# Revit family: HV3 für Kältefestpunkt_
name_source: partatom
category: Allgemeines Modell
revit_build: Autodesk Revit 2017 (Build: 20190508_0315(x64)
units: mm (PartAtom-declared; Revit-internal decimal feet)

## family parameters
Basisbauteil = Fläche
Beim Laden mit Abzugskörper schneiden = Nein
Bemaßung runder Anschluss = Durchmesser verwenden
Gemeinsam genutzt = Ja
Kann Basisbauteil für Bewehrung sein = Nein
Raumberechnungspunkt = Nein
Teiletyp = Normal

## types (2) — shared parameters
Anzahl Rohrschellen = 3
Anzugsmoment Hammersperrkopf = 120 Nm
Artikelnummer = 00200407/fvz
Breite Material Rohrschelle = 50 mm
EAN = 4250928400024
Fabrikat = MEFA
Gewicht = 5.68 kg
Kurztext1 = Festpunkthalterung HV 3
Kurztext2 = 64 - 406 mm Fx 30 kN 164 - 216 mm
Länge = 160 mm  [stored 0.524934 ft]
Mengeneinheit = St
Rohrschellentyp = Titan HD
Stärke Material Rohrschelle = 5 mm
Vorgabe-Ansicht = 1219 mm
max. Achshöhe = 216 mm
max. Rohraußendurchmesser = 406 mm  [stored 1.33202 ft]
max. zul. Last Fx = 6.74 kip
max. zul. Last Fz = 4.05 kip
max. zul. Last Fz mit 3 Schellen = 40 kN
min. Achshöhe = 164 mm
min. Rohraußendurchmesser = 64 mm  [stored 0.209974 ft]
vpe = 1

## per-type parameters (varying)
| type | S |
| HV3 für Kältefestpunkt Ø219,1 mm | 349 mm |
| HV3 für Kältefestpunkt Ø273 mm | 404 mm  [stored 1.32546 ft] |

note: [stored X ft] marks values corroborated as IEEE doubles in the binary element streams (Revit-internal decimal feet)

## geometry (parser evidence)
native form markers: Sweep x5
no freeform markers — native parametric forms only
